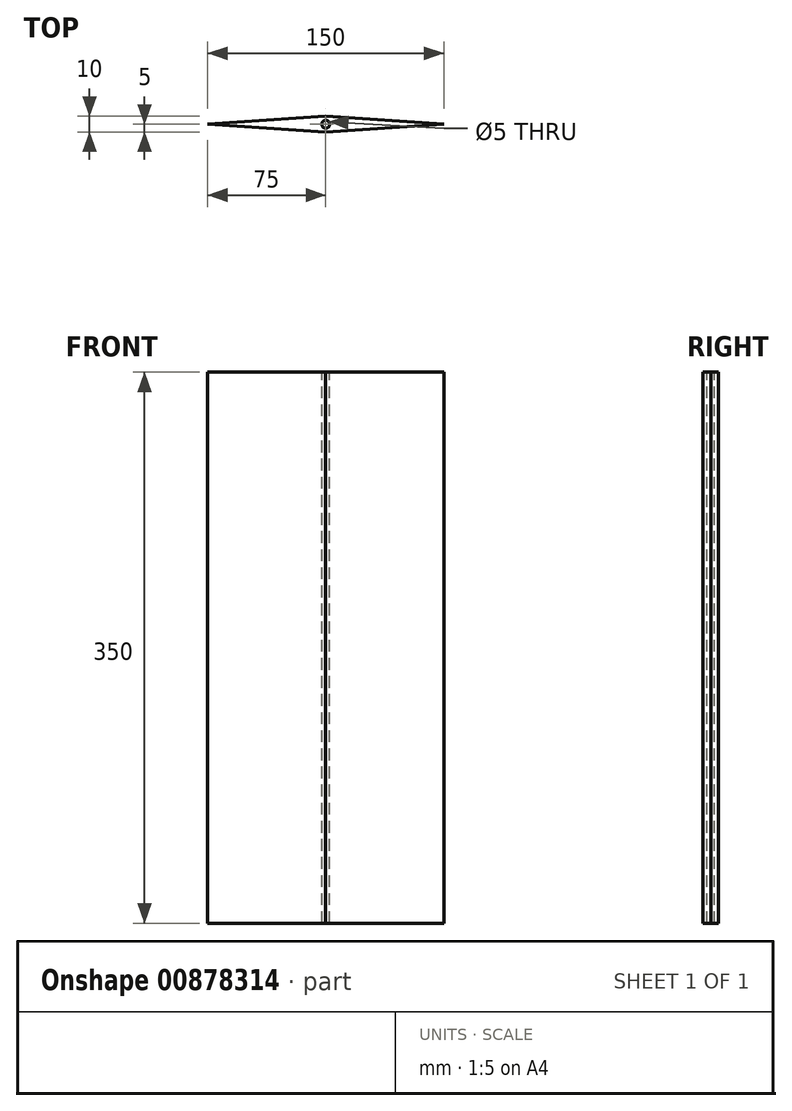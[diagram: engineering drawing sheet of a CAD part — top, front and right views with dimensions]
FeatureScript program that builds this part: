
annotation { "Feature Type Name" : "Feature", "Feature Type Description" : "" }
export const myFeature = defineFeature(function(context is Context, id is Id, definition is map)
    precondition{}
    {
        {
            var Q0;
            Q0=qCreatedBy(makeId("Top.planeOp"),FACE);
            var sketch = newSketch(context, id + "F0", { "sketchPlane" : qUnion([Q0])});
            skLineSegment(sketch, "E0", {"start": v(0, 5) * mm, "end": v(-75, 0) * mm});
            skLineSegment(sketch, "E1.MirrorCS", {"start": v(0, -5) * mm, "end": v(-75, 0) * mm});
            skLineSegment(sketch, "E2.MirrorCS", {"start": v(0, 5) * mm, "end": v(75, 0) * mm});
            skLineSegment(sketch, "E3.MirrorCS", {"start": v(0, -5) * mm, "end": v(75, 0) * mm});
            skSolve(sketch);
        }
        {
            var Q0;
            Q0 = qSketchRegion(id + "F0", true);
            extrude(context, id + "F1", {"entities" : qUnion([Q0]), "endBound" : BoundingType.SYMMETRIC, "depth" : 350 * mm, "offsetDistance" : 25 * mm});
        }
        {
            var Q0;
            Q0=makeQuery(id+"F1.opExtrude","CAP_FACE",FACE,{"disambiguationData":[OSD([sQuery(id+"F0.wireOp",EDGE,"E0"),sQuery(id+"F0.wireOp",EDGE,"E1.MirrorCS"),sQuery(id+"F0.wireOp",EDGE,"E2.MirrorCS"),sQuery(id+"F0.wireOp",EDGE,"E3.MirrorCS")])],"isStart":false});
            var sketch = newSketch(context, id + "F2", { "sketchPlane" : qUnion([Q0])});
            skCircle(sketch, "E4", {"center": v(0, 0) * mm, "radius": 2.5 * mm});
            skSolve(sketch);
        }
        {
            var Q0;
            Q0 = qSketchRegion(id + "F2", true);
            extrude(context, id + "F3", {"entities" : qUnion([Q0]), "operationType" : NewBodyOperationType.REMOVE, "endBound" : BoundingType.UP_TO_NEXT, "oppositeDirection" : true, "depth" : 25 * mm, "offsetDistance" : 25 * mm});
        }
    });
